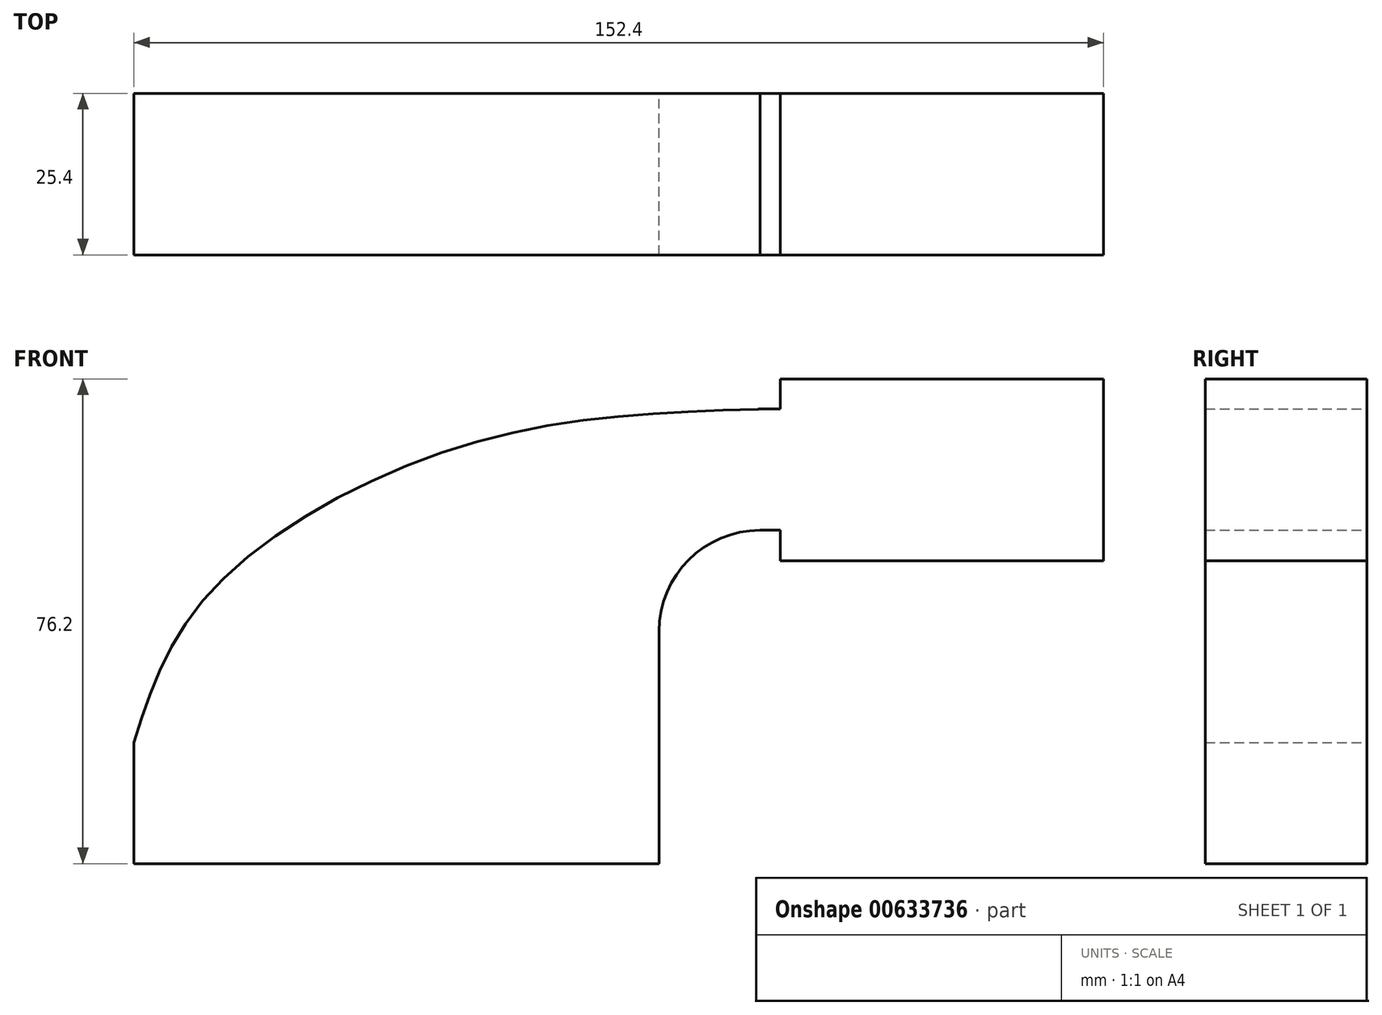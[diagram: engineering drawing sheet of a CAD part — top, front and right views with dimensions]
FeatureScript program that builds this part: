
annotation { "Feature Type Name" : "Feature", "Feature Type Description" : "" }
export const myFeature = defineFeature(function(context is Context, id is Id, definition is map)
    precondition{}
    {
        {
            var Q0;
            Q0=qCreatedBy(makeId("Front.planeOp"),FACE);
            var sketch = newSketch(context, id + "F0", { "sketchPlane" : qUnion([Q0])});
            skLineSegment(sketch, "E0", {"start": v(0, 0) * mm, "end": v(0, -19.05) * mm});
            skLineSegment(sketch, "E1", {"start": v(0, -19.05) * mm, "end": v(-82.55, -19.05) * mm});
            skLineSegment(sketch, "E2", {"start": v(-82.55, -19.05) * mm, "end": v(-82.55, 0) * mm});
            skLineSegment(sketch, "E3", {"start": v(-82.55, 0) * mm, "end": v(0, 0) * mm});
            skLineSegment(sketch, "E4", {"start": v(0, 0) * mm, "end": v(-18.22, 0) * mm});
            skLineSegment(sketch, "E5", {"start": v(-18.22, 0) * mm, "end": v(-18.22, 17.48) * mm});
            skLineSegment(sketch, "E6", {"start": v(0, 0) * mm, "end": v(0, 17.48) * mm});
            skLineSegment(sketch, "E7", {"start": v(0, -19.05) * mm, "end": v(44.45, -19.05) * mm});
            skLineSegment(sketch, "E8", {"start": v(44.45, 57.15) * mm, "end": v(44.45, 28.58) * mm});
            skLineSegment(sketch, "E9", {"start": v(44.45, 28.58) * mm, "end": v(19.05, 28.58) * mm});
            skLineSegment(sketch, "E10", {"start": v(19.05, 28.58) * mm, "end": v(69.85, 28.58) * mm});
            skLineSegment(sketch, "E11", {"start": v(19.05, 28.58) * mm, "end": v(19.05, 57.15) * mm});
            skLineSegment(sketch, "E12", {"start": v(19.05, 57.15) * mm, "end": v(69.85, 57.15) * mm});
            skLineSegment(sketch, "E13", {"start": v(44.45, 33.35) * mm, "end": v(15.87, 33.35) * mm});
            skLineSegment(sketch, "E14", {"start": v(15.87, 33.35) * mm, "end": v(15.87, 52.4) * mm});
            skLineSegment(sketch, "E15", {"start": v(15.87, 52.4) * mm, "end": v(44.45, 52.4) * mm});
            skLineSegment(sketch, "E16", {"start": v(44.45, 52.4) * mm, "end": v(44.45, 33.35) * mm});
            skLineSegment(sketch, "E17", {"start": v(69.85, 57.15) * mm, "end": v(69.85, 28.58) * mm});
            skArc(sketch, "E18", {"start": v(15.87, 33.35) * mm, "mid": v(4.65, 28.7) * mm, "end": v(0, 17.48) * mm});
            skArc(sketch, "E19", {"start": v(15.87, 52.4) * mm, "mid": v(-8.28, 41.88) * mm, "end": v(-18.22, 17.48) * mm});
            skFitSpline(sketch, "E20", {"points": [v(-82.55, 0) * mm, v(-70.97, 23.14) * mm, v(-30.3, 46.8) * mm, v(15.87, 52.4) * mm], "startDerivative": vector(27.9, 87.27) * mm, "endDerivative": vector(126, 3.77) * mm});
            skSolve(sketch);
        }
        {
            var Q0;
            Q0 = qSketchRegion(id + "F0", true);
            extrude(context, id + "F1", {"entities" : qUnion([Q0]), "depth" : 25.4 * mm, "offsetDistance" : 25.4 * mm});
        }
    });
